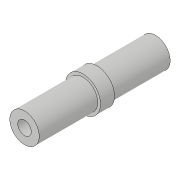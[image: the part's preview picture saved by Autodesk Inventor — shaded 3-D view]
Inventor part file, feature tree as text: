
AUTODESK INVENTOR PART (.ipt)
format: ipt  version: 2018.3 (Build 223284000, 284)  size: 98,304 bytes
history: native  units: in
note: dims shown in document units (in); Inventor stores cm internally (conversion verified against a paired STEP export)
features: extrude x4, sketch x4
ambient origin geometry x8: Origin, YZ Plane, XZ Plane, XY Plane, X Axis, Y Axis, Z Axis, Center Point
bodies: Solid1 (feature_tree)
feature tree (8):
  extrude  "Extrusion1"  Depth=1.87in TaperAngle=0.0deg
  extrude  "Extrusion2"  Depth=0.835in TaperAngle=0.0deg
  extrude  "Extrusion3"  Depth=0.835in TaperAngle=0.0deg
  extrude  "Extrusion4"  Depth=0.835in TaperAngle=0.0deg
  sketch  "Sketch1"  dims[d0=0.5in d2=1.87in d3=0.0in]
  sketch  "Sketch2"  dims[d4=0.42in d5=0.835in d6=0.0in]
  sketch  "Sketch3"  dims[d7=0.42in d8=0.835in d9=0.0in]
  sketch  "Sketch4"  dims[d10=0.1925in d11=0.835in d12=0.0in]
